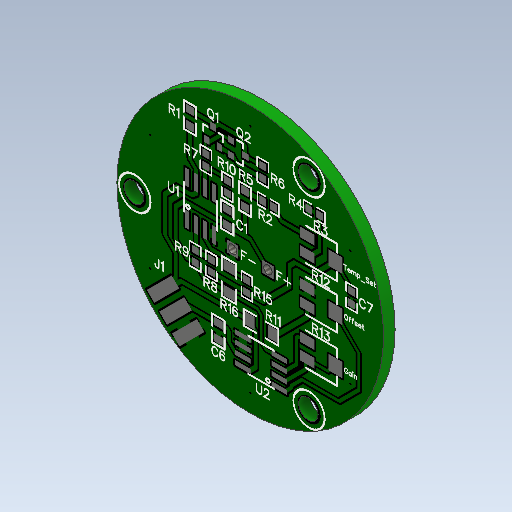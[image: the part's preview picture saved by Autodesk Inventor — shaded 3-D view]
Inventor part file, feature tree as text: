
AUTODESK INVENTOR PART (.ipt)
format: ipt  version: 2020 (Build 240168000, 168)  size: 223,744 bytes
history: native  units: in
note: dims shown in document units (in); Inventor stores cm internally (conversion verified against a paired STEP export)
features: other x4, sketch x4, extrude x2
ambient origin geometry x8: Origin, YZ Plane, XZ Plane, XY Plane, X Axis, Y Axis, Z Axis, Center Point
bodies: Solid1 (feature_tree)
feature tree (10):
  extrude  "Extrusion1"  Depth=0.065in TaperAngle=0.0deg
  other  "Decal1"
  extrude  "Extrusion2"  Depth=1.5in
  other  "Decal3"
  sketch  "Sketch1"  dims[d0=1.5in d1=0.065in d2=0.0in]
  sketch  "Sketch2"  dims[d8=0.11in d9=1.5in]
  sketch  "Sketch3"  dims[d11=0.75in]
  sketch  "Sketch5"  dims[d13=0.048in d14=0.2in d15=0.1in d16=0.0in d17=0.0in d25=0.98in d26=0.0967in]
  other  "Image4"
  other  "Image5"
